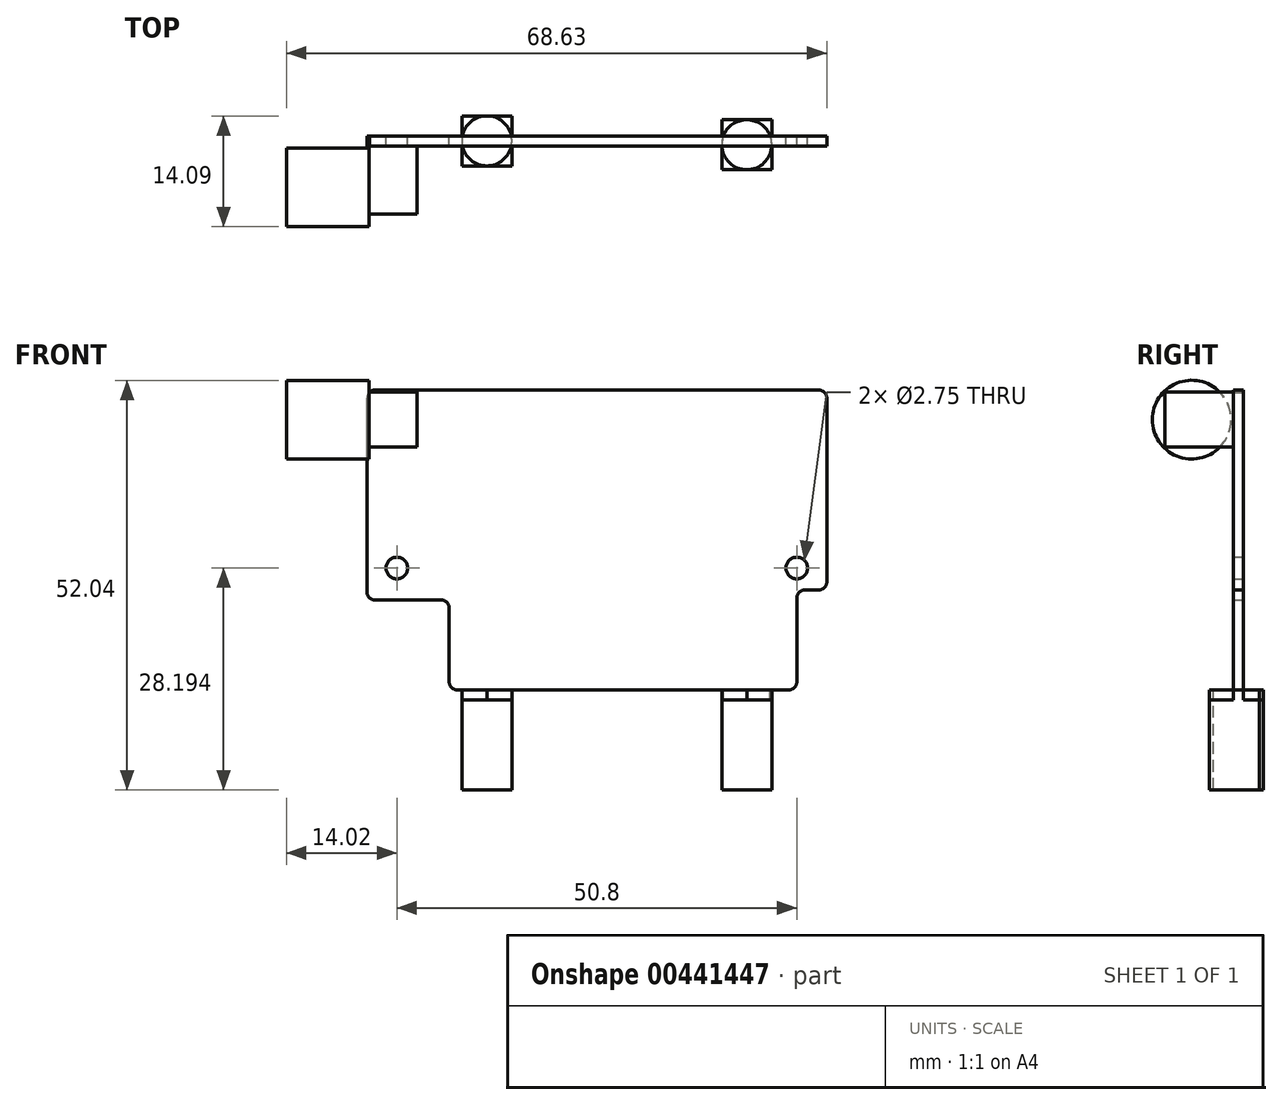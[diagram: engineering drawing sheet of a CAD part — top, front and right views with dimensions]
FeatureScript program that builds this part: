
annotation { "Feature Type Name" : "Feature", "Feature Type Description" : "" }
export const myFeature = defineFeature(function(context is Context, id is Id, definition is map)
    precondition{}
    {
        {
            var Q0;
            Q0=qCreatedBy(makeId("Front.planeOp"),FACE);
            var sketch = newSketch(context, id + "F0", { "sketchPlane" : qUnion([Q0])});
            skLineSegment(sketch, "E0", {"start": v(10.46, 1.02) * mm, "end": v(10.46, 10.41) * mm});
            skLineSegment(sketch, "E1", {"start": v(9.45, 11.43) * mm, "end": v(1.02, 11.43) * mm});
            skLineSegment(sketch, "E2", {"start": v(0, 12.45) * mm, "end": v(0, 37.08) * mm});
            skLineSegment(sketch, "E3", {"start": v(1.02, 38.1) * mm, "end": v(57.4, 38.1) * mm});
            skLineSegment(sketch, "E4", {"start": v(58.42, 37.08) * mm, "end": v(58.42, 13.72) * mm});
            skLineSegment(sketch, "E5", {"start": v(57.4, 12.7) * mm, "end": v(55.63, 12.7) * mm});
            skLineSegment(sketch, "E6", {"start": v(54.61, 11.68) * mm, "end": v(54.61, 1.02) * mm});
            skLineSegment(sketch, "E7", {"start": v(53.6, 0) * mm, "end": v(11.48, 0) * mm});
            skPoint(sketch, "E8.visualSharp", {"position": v(58.42, 38.1) * mm});
            skArc(sketch, "E8.filletArc", {"start": v(58.42, 37.08) * mm, "mid": v(58.12, 37.8) * mm, "end": v(57.4, 38.1) * mm});
            skPoint(sketch, "E9.visualSharp", {"position": v(0, 38.1) * mm});
            skArc(sketch, "E9.filletArc", {"start": v(1.02, 38.1) * mm, "mid": v(0.3, 37.8) * mm, "end": v(0, 37.08) * mm});
            skPoint(sketch, "E10.visualSharp", {"position": v(0, 11.43) * mm});
            skArc(sketch, "E10.filletArc", {"start": v(0, 12.45) * mm, "mid": v(0.3, 11.73) * mm, "end": v(1.02, 11.43) * mm});
            skPoint(sketch, "E11.visualSharp", {"position": v(10.46, 11.43) * mm});
            skArc(sketch, "E11.filletArc", {"start": v(10.46, 10.41) * mm, "mid": v(10.17, 11.13) * mm, "end": v(9.45, 11.43) * mm});
            skPoint(sketch, "E12.visualSharp", {"position": v(10.46, 0) * mm});
            skArc(sketch, "E12.filletArc", {"start": v(10.46, 1.02) * mm, "mid": v(10.76, 0.3) * mm, "end": v(11.48, 0) * mm});
            skPoint(sketch, "E13.visualSharp", {"position": v(54.61, 0) * mm});
            skArc(sketch, "E13.filletArc", {"start": v(53.6, 0) * mm, "mid": v(54.31, 0.3) * mm, "end": v(54.61, 1.02) * mm});
            skPoint(sketch, "E14.visualSharp", {"position": v(54.61, 12.7) * mm});
            skArc(sketch, "E14.filletArc", {"start": v(55.63, 12.7) * mm, "mid": v(54.9, 12.4) * mm, "end": v(54.61, 11.68) * mm});
            skPoint(sketch, "E15.visualSharp", {"position": v(58.42, 12.7) * mm});
            skArc(sketch, "E15.filletArc", {"start": v(57.4, 12.7) * mm, "mid": v(58.12, 13) * mm, "end": v(58.42, 13.72) * mm});
            skCircle(sketch, "E16", {"center": v(3.8, 15.5) * mm, "radius": 1.37 * mm});
            skCircle(sketch, "E17", {"center": v(54.61, 15.5) * mm, "radius": 1.37 * mm});
            skSolve(sketch);
        }
        {
            var Q0;
            Q0=makeQuery(id+"F0.imprint","IMPRINT",FACE,{"disambiguationData":[TD([[makeQuery(id+"F0.imprint","IMPRINT",EDGE,{"derivedFrom":sQuery(id+"F0.wireOp",EDGE,"E0")}),-1.0]])]});
            extrude(context, id + "F1", {"entities" : qUnion([Q0]), "depth" : 1.27 * mm});
        }
        {
            var Q0;
            Q0=makeQuery(id+"F1.opExtrude","SWEPT_FACE",FACE,{"disambiguationData":[OSD([sQuery(id+"F0.wireOp",EDGE,"E7")])]});
            var sketch = newSketch(context, id + "F2", { "sketchPlane" : qUnion([Q0])});
            skLineSegment(sketch, "E18.bottom", {"start": v(18.41, -2.54) * mm, "end": v(12.07, -2.54) * mm});
            skLineSegment(sketch, "E18.top", {"start": v(18.41, 3.81) * mm, "end": v(12.07, 3.81) * mm});
            skLineSegment(sketch, "E18.left", {"start": v(18.41, -2.54) * mm, "end": v(18.41, 3.81) * mm});
            skLineSegment(sketch, "E18.right", {"start": v(12.06, -2.54) * mm, "end": v(12.06, 3.81) * mm});
            skPoint(sketch, "E18.middle", {"position": v(15.24, 0.64) * mm});
            skLineSegment(sketch, "E19.bottom", {"start": v(51.44, -2.04) * mm, "end": v(45.09, -2.04) * mm});
            skLineSegment(sketch, "E19.top", {"start": v(51.44, 4.3) * mm, "end": v(45.09, 4.3) * mm});
            skLineSegment(sketch, "E19.left", {"start": v(51.44, -2.04) * mm, "end": v(51.44, 4.3) * mm});
            skLineSegment(sketch, "E19.right", {"start": v(45.09, -2.04) * mm, "end": v(45.09, 4.3) * mm});
            skPoint(sketch, "E19.middle", {"position": v(48.26, 1.13) * mm});
            skCircle(sketch, "E20", {"center": v(15.24, 0.64) * mm, "radius": 3.18 * mm});
            skCircle(sketch, "E21", {"center": v(48.26, 1.13) * mm, "radius": 3.17 * mm});
            skSolve(sketch);
        }
        {
            var Q0;
            {var subQ0=sQuery(id+"F2.wireOp",EDGE,"E18.left");var subQ1=sQuery(id+"F2.wireOp",EDGE,"E18.top");var subQ2=makeQuery(id+"F2.imprint","INTERSECT",VERTEX,{"derivedFrom":[subQ1,subQ0]});Q0=makeQuery(id+"F2.imprint","IMPRINT",FACE,{"disambiguationData":[TD([[makeQuery(id+"F2.imprint","IMPRINT",EDGE,{"disambiguationData":[TD([[subQ2,-1.0]])],"derivedFrom":subQ1}),1.0]])]});}
            var Q1;
            {var subQ0=sQuery(id+"F2.wireOp",EDGE,"E18.right");var subQ1=sQuery(id+"F2.wireOp",EDGE,"E18.top");var subQ2=makeQuery(id+"F2.imprint","INTERSECT",VERTEX,{"derivedFrom":[subQ1,subQ0]});Q1=makeQuery(id+"F2.imprint","IMPRINT",FACE,{"disambiguationData":[TD([[makeQuery(id+"F2.imprint","IMPRINT",EDGE,{"disambiguationData":[TD([[subQ2,1.0]])],"derivedFrom":subQ1}),1.0]])]});}
            var Q2;
            {var subQ0=sQuery(id+"F2.wireOp",EDGE,"E18.right");var subQ1=sQuery(id+"F2.wireOp",EDGE,"E18.bottom");var subQ2=makeQuery(id+"F2.imprint","INTERSECT",VERTEX,{"derivedFrom":[subQ1,subQ0]});Q2=makeQuery(id+"F2.imprint","IMPRINT",FACE,{"disambiguationData":[TD([[makeQuery(id+"F2.imprint","IMPRINT",EDGE,{"disambiguationData":[TD([[subQ2,1.0]])],"derivedFrom":subQ1}),-1.0]])]});}
            var Q3;
            {var subQ0=sQuery(id+"F2.wireOp",EDGE,"E18.left");var subQ1=sQuery(id+"F2.wireOp",EDGE,"E18.bottom");var subQ2=makeQuery(id+"F2.imprint","INTERSECT",VERTEX,{"derivedFrom":[subQ1,subQ0]});Q3=makeQuery(id+"F2.imprint","IMPRINT",FACE,{"disambiguationData":[TD([[makeQuery(id+"F2.imprint","IMPRINT",EDGE,{"disambiguationData":[TD([[subQ2,-1.0]])],"derivedFrom":subQ1}),-1.0]])]});}
            var Q4;
            {var subQ0=sQuery(id+"F2.wireOp",EDGE,"E19.left");var subQ1=sQuery(id+"F2.wireOp",EDGE,"E19.top");var subQ2=makeQuery(id+"F2.imprint","INTERSECT",VERTEX,{"derivedFrom":[subQ1,subQ0]});Q4=makeQuery(id+"F2.imprint","IMPRINT",FACE,{"disambiguationData":[TD([[makeQuery(id+"F2.imprint","IMPRINT",EDGE,{"disambiguationData":[TD([[subQ2,-1.0]])],"derivedFrom":subQ1}),1.0]])]});}
            var Q5;
            {var subQ0=sQuery(id+"F2.wireOp",EDGE,"E19.right");var subQ1=sQuery(id+"F2.wireOp",EDGE,"E19.top");var subQ2=makeQuery(id+"F2.imprint","INTERSECT",VERTEX,{"derivedFrom":[subQ1,subQ0]});Q5=makeQuery(id+"F2.imprint","IMPRINT",FACE,{"disambiguationData":[TD([[makeQuery(id+"F2.imprint","IMPRINT",EDGE,{"disambiguationData":[TD([[subQ2,1.0]])],"derivedFrom":subQ1}),1.0]])]});}
            var Q6;
            {var subQ0=sQuery(id+"F2.wireOp",EDGE,"E19.right");var subQ1=sQuery(id+"F2.wireOp",EDGE,"E19.bottom");var subQ2=makeQuery(id+"F2.imprint","INTERSECT",VERTEX,{"derivedFrom":[subQ1,subQ0]});Q6=makeQuery(id+"F2.imprint","IMPRINT",FACE,{"disambiguationData":[TD([[makeQuery(id+"F2.imprint","IMPRINT",EDGE,{"disambiguationData":[TD([[subQ2,1.0]])],"derivedFrom":subQ1}),-1.0]])]});}
            var Q7;
            {var subQ0=sQuery(id+"F2.wireOp",EDGE,"E19.left");var subQ1=sQuery(id+"F2.wireOp",EDGE,"E19.bottom");var subQ2=makeQuery(id+"F2.imprint","INTERSECT",VERTEX,{"derivedFrom":[subQ1,subQ0]});Q7=makeQuery(id+"F2.imprint","IMPRINT",FACE,{"disambiguationData":[TD([[makeQuery(id+"F2.imprint","IMPRINT",EDGE,{"disambiguationData":[TD([[subQ2,-1.0]])],"derivedFrom":subQ1}),-1.0]])]});}
            extrude(context, id + "F3", {"entities" : qUnion([Q0, Q1, Q2, Q3, Q4, Q5, Q6, Q7]), "depth" : 1.27 * mm});
        }
        {
            var Q0;
            {var subQ0=sQuery(id+"F2.wireOp",EDGE,"E20");var subQ1=makeQuery(id+"F2.imprint","INTERSECT",VERTEX,{"derivedFrom":[sQuery(id+"F2.wireOp",EDGE,"E18.top"),subQ0]});Q0=makeQuery(id+"F2.imprint","IMPRINT",FACE,{"disambiguationData":[TD([[makeQuery(id+"F2.imprint","IMPRINT",EDGE,{"disambiguationData":[TD([[subQ1,1.0]])],"derivedFrom":subQ0}),1.0]])]});}
            var Q1;
            {var subQ0=sQuery(id+"F2.wireOp",EDGE,"E20");var subQ1=makeQuery(id+"F2.imprint","INTERSECT",VERTEX,{"derivedFrom":[sQuery(id+"F2.wireOp",EDGE,"E18.left"),subQ0]});Q1=makeQuery(id+"F2.imprint","IMPRINT",FACE,{"disambiguationData":[TD([[makeQuery(id+"F2.imprint","IMPRINT",EDGE,{"disambiguationData":[TD([[subQ1,-1.0]])],"derivedFrom":subQ0}),1.0]])]});}
            var Q2;
            {var subQ0=sQuery(id+"F2.wireOp",EDGE,"E20");var subQ1=makeQuery(id+"F2.imprint","INTERSECT",VERTEX,{"derivedFrom":[sQuery(id+"F2.wireOp",EDGE,"E18.bottom"),subQ0]});Q2=makeQuery(id+"F2.imprint","IMPRINT",FACE,{"disambiguationData":[TD([[makeQuery(id+"F2.imprint","IMPRINT",EDGE,{"disambiguationData":[TD([[subQ1,1.0]])],"derivedFrom":subQ0}),1.0]])]});}
            var Q3;
            {var subQ0=sQuery(id+"F2.wireOp",EDGE,"E21");var subQ1=makeQuery(id+"F2.imprint","INTERSECT",VERTEX,{"derivedFrom":[sQuery(id+"F2.wireOp",EDGE,"E19.top"),subQ0]});Q3=makeQuery(id+"F2.imprint","IMPRINT",FACE,{"disambiguationData":[TD([[makeQuery(id+"F2.imprint","IMPRINT",EDGE,{"disambiguationData":[TD([[subQ1,1.0]])],"derivedFrom":subQ0}),1.0]])]});}
            var Q4;
            {var subQ0=sQuery(id+"F2.wireOp",EDGE,"E21");var subQ1=makeQuery(id+"F2.imprint","INTERSECT",VERTEX,{"derivedFrom":[sQuery(id+"F2.wireOp",EDGE,"E19.left"),subQ0]});Q4=makeQuery(id+"F2.imprint","IMPRINT",FACE,{"disambiguationData":[TD([[makeQuery(id+"F2.imprint","IMPRINT",EDGE,{"disambiguationData":[TD([[subQ1,-1.0]])],"derivedFrom":subQ0}),1.0]])]});}
            var Q5;
            {var subQ0=sQuery(id+"F2.wireOp",EDGE,"E21");var subQ1=makeQuery(id+"F2.imprint","INTERSECT",VERTEX,{"derivedFrom":[sQuery(id+"F2.wireOp",EDGE,"E19.bottom"),subQ0]});Q5=makeQuery(id+"F2.imprint","IMPRINT",FACE,{"disambiguationData":[TD([[makeQuery(id+"F2.imprint","IMPRINT",EDGE,{"disambiguationData":[TD([[subQ1,1.0]])],"derivedFrom":subQ0}),1.0]])]});}
            extrude(context, id + "F4", {"entities" : qUnion([Q0, Q1, Q2, Q3, Q4, Q5]), "depth" : 12.7 * mm});
        }
        {
            var Q0;
            Q0=makeQuery(id+"F1.opExtrude","CAP_FACE",FACE,{"disambiguationData":[OSD([sQuery(id+"F0.wireOp",EDGE,"E0"),sQuery(id+"F0.wireOp",EDGE,"E1"),sQuery(id+"F0.wireOp",EDGE,"E2"),sQuery(id+"F0.wireOp",EDGE,"E3"),sQuery(id+"F0.wireOp",EDGE,"E4"),sQuery(id+"F0.wireOp",EDGE,"E5"),sQuery(id+"F0.wireOp",EDGE,"E6"),sQuery(id+"F0.wireOp",EDGE,"E7"),sQuery(id+"F0.wireOp",EDGE,"E8.filletArc"),sQuery(id+"F0.wireOp",EDGE,"E9.filletArc"),sQuery(id+"F0.wireOp",EDGE,"E10.filletArc"),sQuery(id+"F0.wireOp",EDGE,"E11.filletArc"),sQuery(id+"F0.wireOp",EDGE,"E12.filletArc"),sQuery(id+"F0.wireOp",EDGE,"E13.filletArc"),sQuery(id+"F0.wireOp",EDGE,"E14.filletArc"),sQuery(id+"F0.wireOp",EDGE,"E15.filletArc"),sQuery(id+"F0.wireOp",EDGE,"E16"),sQuery(id+"F0.wireOp",EDGE,"E17")])],"isStart":true});
            var sketch = newSketch(context, id + "F5", { "sketchPlane" : qUnion([Q0])});
            skLineSegment(sketch, "E22.bottom", {"start": v(-6.4, 37.85) * mm, "end": v(-0.3, 37.85) * mm});
            skLineSegment(sketch, "E22.top", {"start": v(-6.4, 30.84) * mm, "end": v(-0.3, 30.84) * mm});
            skLineSegment(sketch, "E22.left", {"start": v(-6.4, 37.85) * mm, "end": v(-6.4, 30.84) * mm});
            skLineSegment(sketch, "E22.right", {"start": v(-0.3, 37.85) * mm, "end": v(-0.3, 30.84) * mm});
            skSolve(sketch);
        }
        {
            var Q0;
            Q0 = qSketchRegion(id + "F5", true);
            extrude(context, id + "F6", {"entities" : qUnion([Q0]), "operationType" : NewBodyOperationType.ADD, "depth" : -9.93 * mm});
        }
        {
            var Q0;
            Q0=makeQuery(id+"F6.opExtrude","SWEPT_FACE",FACE,{"disambiguationData":[OSD([sQuery(id+"F5.wireOp",EDGE,"E22.right")])]});
            var sketch = newSketch(context, id + "F7", { "sketchPlane" : qUnion([Q0])});
            skCircle(sketch, "E23", {"center": v(6.55, 34.34) * mm, "radius": 5 * mm});
            skPoint(sketch, "E23.centerSnap0", {"position": v(9.93, 34.34) * mm});
            skSolve(sketch);
        }
        {
            var Q0;
            Q0 = qSketchRegion(id + "F7", true);
            extrude(context, id + "F8", {"entities" : qUnion([Q0]), "operationType" : NewBodyOperationType.ADD, "depth" : 10.52 * mm});
        }
    });
